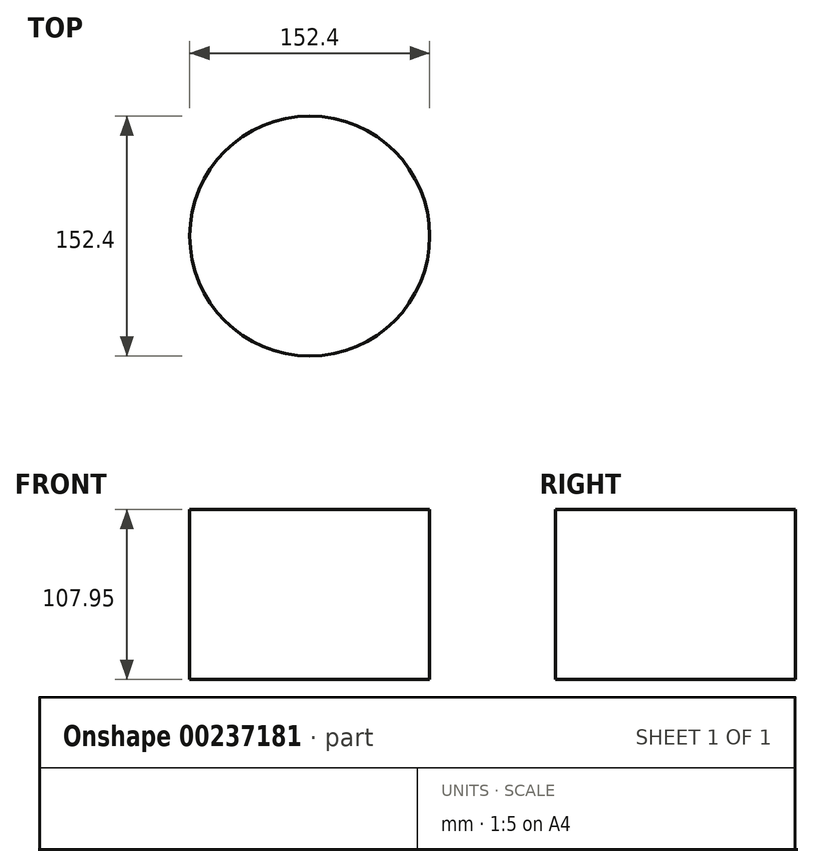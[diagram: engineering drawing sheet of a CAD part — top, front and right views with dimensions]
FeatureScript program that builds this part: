
annotation { "Feature Type Name" : "Feature", "Feature Type Description" : "" }
export const myFeature = defineFeature(function(context is Context, id is Id, definition is map)
    precondition{}
    {
        {
            var Q0;
            Q0=qCreatedBy(makeId("Top.planeOp"),FACE);
            var sketch = newSketch(context, id + "F0", { "sketchPlane" : qUnion([Q0])});
            skCircle(sketch, "E0", {"center": v(-56.81, -50.78) * mm, "radius": 76.2 * mm});
            skPoint(sketch, "E0.first.point", {"position": v(-106.36, -108.67) * mm});
            skPoint(sketch, "E0.second.point", {"position": v(0, 0) * mm});
            skPoint(sketch, "E0.third.point", {"position": v(18.83, -41.56) * mm});
            skSolve(sketch);
        }
        {
            var Q0;
            Q0=makeQuery(id+"F0.imprint","IMPRINT",FACE,{"disambiguationData":[TD([[makeQuery(id+"F0.imprint","IMPRINT",EDGE,{"derivedFrom":sQuery(id+"F0.wireOp",EDGE,"E0")}),1.0]])]});
            extrude(context, id + "F1", {"entities" : qUnion([Q0]), "depth" : 107.95 * mm});
        }
    });
